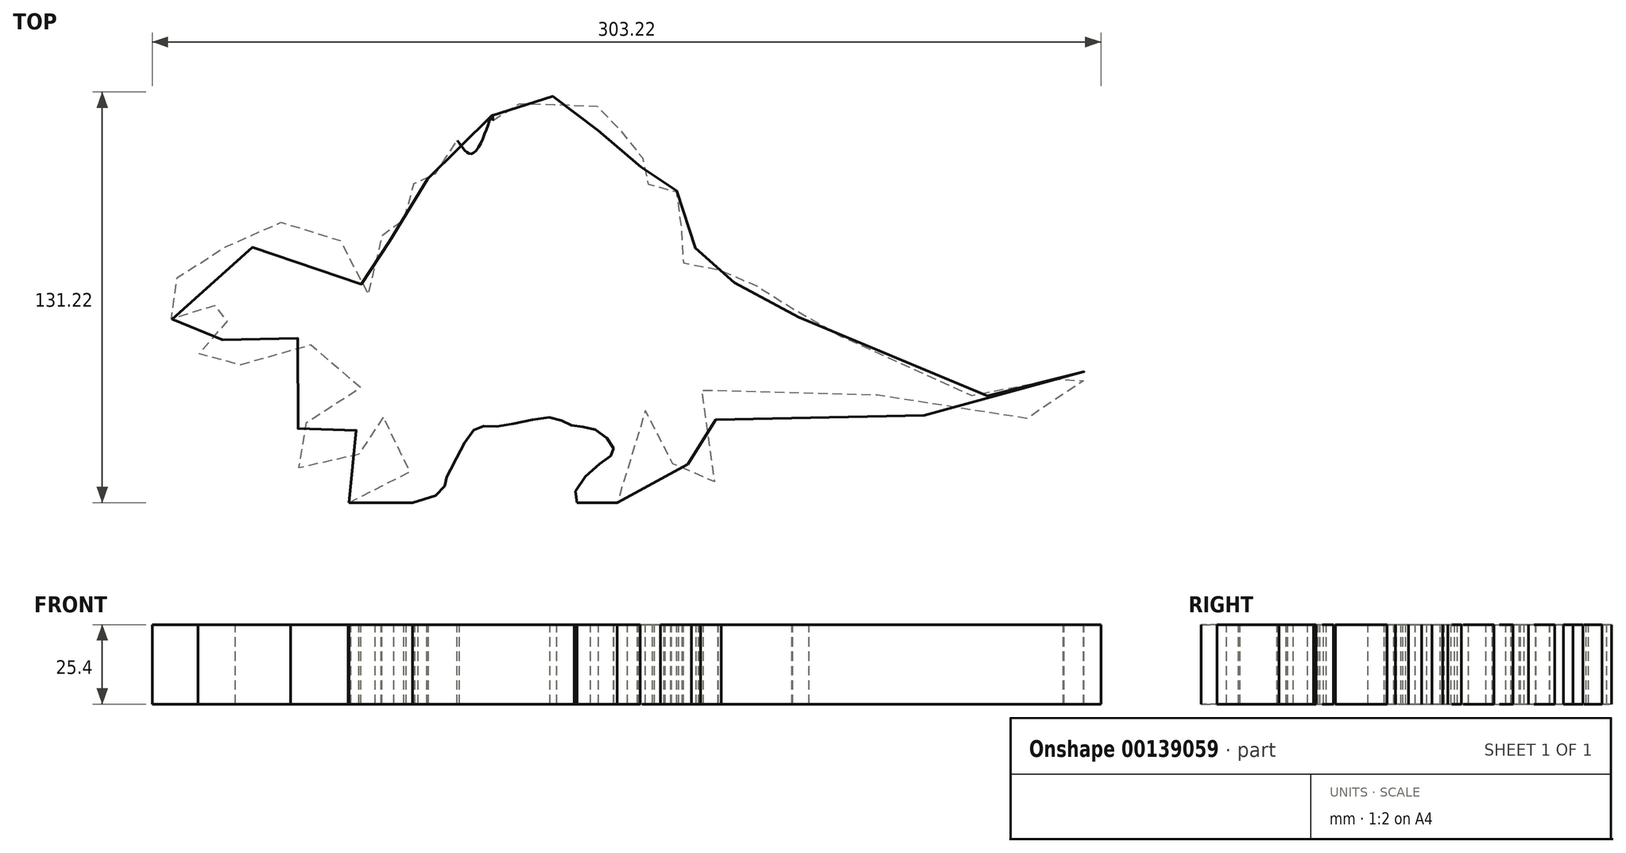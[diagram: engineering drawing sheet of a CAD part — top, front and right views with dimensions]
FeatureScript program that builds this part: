
annotation { "Feature Type Name" : "Feature", "Feature Type Description" : "" }
export const myFeature = defineFeature(function(context is Context, id is Id, definition is map)
    precondition{}
    {
        {
            var Q0;
            Q0=qCreatedBy(makeId("Top.planeOp"),FACE);
            var sketch = newSketch(context, id + "F0", { "sketchPlane" : qUnion([Q0])});
            skFitSpline(sketch, "E0", {"points": [v(-218.87, 56.4) * mm, v(-203.12, 63.8) * mm, v(-201.27, 69.36) * mm, v(-189.23, 69.05) * mm, v(-183.67, 74.3) * mm, v(-171.94, 78.93) * mm, v(-163.3, 74.6) * mm, v(-155.26, 65.34) * mm, v(-152.8, 56.7) * mm, v(-148.47, 53.3) * mm, v(-146.93, 56.4) * mm, v(-148.47, 65.65) * mm, v(-142.91, 61.64) * mm, v(-146.62, 73.37) * mm, v(-140.13, 67.81) * mm, v(-139.2, 75.22) * mm, v(-138.9, 82.02) * mm, v(-136.12, 84.49) * mm, v(-136.74, 90.05) * mm, v(-132.1, 86.96) * mm, v(-132.1, 94.68) * mm, v(-126.86, 91.28) * mm, v(-121.92, 96.22) * mm, v(-122.53, 103.63) * mm, v(-117.9, 99.3) * mm, v(-111.42, 111.66) * mm, v(-110.5, 104.25) * mm, v(-107.1, 105.48) * mm, v(-103.08, 117.52) * mm, v(-101.85, 112.58) * mm, v(-95.98, 111.97) * mm, v(-91.04, 119.07) * mm, v(-91.04, 116.29) * mm, v(-92.9, 111.04) * mm, v(-86.1, 110.73) * mm, v(-77.46, 115.98) * mm, v(-79.93, 108.26) * mm, v(-75.91, 107.03) * mm, v(-68.2, 109.8) * mm, v(-72.52, 103.01) * mm, v(-66.96, 99.62) * mm, v(-60.17, 103.63) * mm, v(-64.49, 94.99) * mm, v(-56.15, 100.85) * mm, v(-62.33, 89.74) * mm, v(-54.3, 92.52) * mm, v(-59.55, 85.41) * mm, v(-52.45, 87.58) * mm, v(-56.46, 81.4) * mm, v(-50.6, 81.4) * mm, v(-54, 76.46) * mm, v(-47.82, 73.99) * mm, v(-51.83, 71.21) * mm, v(-46.27, 70.28) * mm, v(-50.29, 64.42) * mm, v(-44.11, 66.58) * mm, v(-44.73, 61.95) * mm, v(-39.48, 65.04) * mm, v(-38.86, 60.1) * mm, v(-34.85, 61.64) * mm, v(-33.3, 56.4) * mm, v(-27.44, 58.24) * mm, v(-25.9, 51.76) * mm, v(-21.88, 54.23) * mm, v(-20.95, 49.9) * mm, v(-15.4, 49.9) * mm, v(-15.4, 47.44) * mm, v(-10.46, 47.13) * mm, v(-9.84, 44.35) * mm, v(7.76, 38.8) * mm, v(31.54, 24.28) * mm, v(58.09, 24.28) * mm, v(61.48, 27.06) * mm, v(67.35, 26.13) * mm, v(71.36, 30.76) * mm, v(71.67, 25.2) * mm, v(77.54, 30.15) * mm, v(78.16, 24.28) * mm, v(83.1, 24.59) * mm, v(64.88, 16.25) * mm, v(29.07, 15.02) * mm, v(-5.2, 27.06) * mm, v(-45.35, 22.74) * mm, v(-40.1, 14.7) * mm, v(-39.79, -4.74) * mm, v(-43.8, -6.29) * mm, v(-56.77, -5.67) * mm, v(-55.84, 0) * mm, v(-49.05, 0) * mm, v(-49.05, 7.6) * mm, v(-62.64, 17.18) * mm, v(-64.49, 3.9) * mm, v(-67.58, -10.3) * mm, v(-84.87, -11.54) * mm, v(-77.46, 0) * mm, v(-72.52, 4.52) * mm, v(-78.07, 11) * mm, v(-85.8, 12.55) * mm, v(-92.59, 15.02) * mm, v(-109.26, 12.24) * mm, v(-116.98, 11.31) * mm, v(-123.77, 0) * mm, v(-125.93, -4.13) * mm, v(-129.02, -9.68) * mm, v(-157.12, -12.15) * mm, v(-154.65, -9.07) * mm, v(-137.97, -2.58) * mm, v(-137.66, 13.47) * mm, v(-151.25, 13.47) * mm, v(-156.5, 7.3) * mm, v(-154.03, 3.28) * mm, v(-164.53, -3.82) * mm, v(-174.1, 0) * mm, v(-175.64, 6.99) * mm, v(-171.94, 12.86) * mm, v(-163.3, 15.63) * mm, v(-153.41, 24.28) * mm, v(-158.66, 27.99) * mm, v(-168.54, 37.56) * mm, v(-182.43, 40.34) * mm, v(-196.64, 28.3) * mm, v(-204.36, 30.76) * mm, v(-204.66, 36.01) * mm, v(-198.49, 38.48) * mm, v(-196.94, 43.11) * mm, v(-194.78, 48.05) * mm, v(-193.55, 50.83) * mm, v(-195.4, 52.38) * mm, v(-202.2, 50.22) * mm, v(-207.75, 50.22) * mm, v(-212.07, 46.82) * mm, v(-217.94, 48.36) * mm, v(-218.87, 56.4) * mm]});
            skLineSegment(sketch, "E1", {"start": v(-165.14, -12.15) * mm, "end": v(-12.3, -12.15) * mm});
            skSolve(sketch);
        }
        {
            var Q0;
            {var subQ0=sQuery(id+"F0.wireOp",EDGE,"E1");var subQ1=sQuery(id+"F0.wireOp",EDGE,"E0");var subQ2=makeQuery(id+"F0.imprint","INTERSECT",VERTEX,{"disambiguationData":[OD(2.0)],"derivedFrom":[subQ1,subQ0]});Q0=makeQuery(id+"F0.imprint","IMPRINT",FACE,{"disambiguationData":[TD([[makeQuery(id+"F0.imprint","IMPRINT",EDGE,{"disambiguationData":[TD([[subQ2,-1.0]])],"derivedFrom":subQ1}),-1.0]])]});}
            extrude(context, id + "F1", {"entities" : qUnion([Q0]), "depth" : 25.4 * mm});
        }
    });
